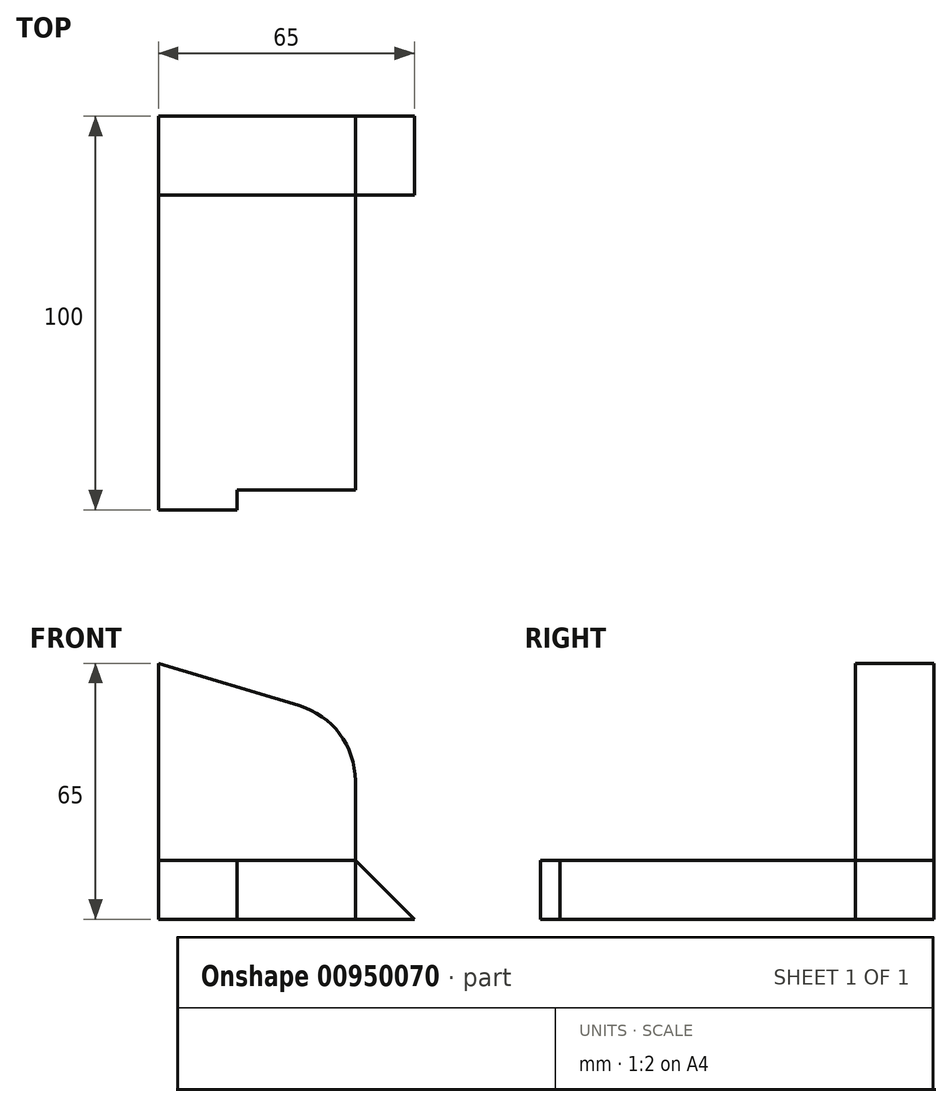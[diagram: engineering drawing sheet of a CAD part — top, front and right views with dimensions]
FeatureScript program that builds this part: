
annotation { "Feature Type Name" : "Feature", "Feature Type Description" : "" }
export const myFeature = defineFeature(function(context is Context, id is Id, definition is map)
    precondition{}
    {
        {
            var Q0;
            Q0=qCreatedBy(makeId("Top.planeOp"),FACE);
            var sketch = newSketch(context, id + "F0", { "sketchPlane" : qUnion([Q0])});
            skLineSegment(sketch, "E0.bottom", {"start": v(0, 0) * mm, "end": v(20, 0) * mm});
            skLineSegment(sketch, "E0.top", {"start": v(0, 100) * mm, "end": v(50, 100) * mm});
            skLineSegment(sketch, "E0.left", {"start": v(0, 0) * mm, "end": v(0, 100) * mm});
            skLineSegment(sketch, "E0.right", {"start": v(50, 5) * mm, "end": v(50, 100) * mm});
            skLineSegment(sketch, "E1.top", {"start": v(20, 5) * mm, "end": v(50, 5) * mm});
            skLineSegment(sketch, "E1.left", {"start": v(20, 0) * mm, "end": v(20, 5) * mm});
            skSolve(sketch);
        }
        {
            var Q0;
            Q0 = qSketchRegion(id + "F0", true);
            extrude(context, id + "F1", {"entities" : qUnion([Q0]), "depth" : 15 * mm, "offsetDistance" : 25 * mm});
        }
        {
            var Q0;
            Q0=makeQuery(id+"F1.opExtrude","SWEPT_FACE",FACE,{"disambiguationData":[OSD([sQuery(id+"F0.wireOp",EDGE,"E0.top")])]});
            var sketch = newSketch(context, id + "F2", { "sketchPlane" : qUnion([Q0])});
            skLineSegment(sketch, "E2", {"start": v(0, 15) * mm, "end": v(0, 65) * mm});
            skLineSegment(sketch, "E3", {"start": v(0, 65) * mm, "end": v(-50, 50) * mm});
            skLineSegment(sketch, "E4", {"start": v(-50, 50) * mm, "end": v(-50, 15) * mm});
            skLineSegment(sketch, "E5", {"start": v(-50, 15) * mm, "end": v(0, 15) * mm});
            skSolve(sketch);
        }
        {
            var Q0;
            Q0 = qSketchRegion(id + "F2", true);
            extrude(context, id + "F3", {"entities" : qUnion([Q0]), "operationType" : NewBodyOperationType.ADD, "oppositeDirection" : true, "depth" : 20 * mm, "offsetDistance" : 25 * mm});
        }
        {
            var Q0;
            Q0=makeQuery(id+"F3.opExtrude","SWEPT_EDGE",EDGE,{"disambiguationData":[OSD([sQuery(id+"F2.wireOp",EDGE,"E3"),sQuery(id+"F2.wireOp",EDGE,"E4")])]});
            fillet(context, id + "F4", {"entities" : qUnion([Q0]), "radius" : 20 * mm, "tangentPropagation" : true, "allowEdgeOverflow" : false});
        }
        {
            var Q0;
            Q0=makeQuery(id+"F3.boolean.opBoolean","MERGE",FACE,{"derivedFrom":[makeQuery(id+"F1.opExtrude","SWEPT_FACE",FACE,{"disambiguationData":[OSD([sQuery(id+"F0.wireOp",EDGE,"E0.top")])]}),makeQuery(id+"F3.opExtrude","CAP_FACE",FACE,{"disambiguationData":[OSD([sQuery(id+"F2.wireOp",EDGE,"E2"),sQuery(id+"F2.wireOp",EDGE,"E3"),sQuery(id+"F2.wireOp",EDGE,"E4"),sQuery(id+"F2.wireOp",EDGE,"E5")])],"isStart":true})]});
            var sketch = newSketch(context, id + "F5", { "sketchPlane" : qUnion([Q0])});
            skLineSegment(sketch, "E6", {"start": v(-50, 0) * mm, "end": v(-50, 15) * mm});
            skLineSegment(sketch, "E7", {"start": v(-50, 15) * mm, "end": v(-65, 0) * mm});
            skLineSegment(sketch, "E8", {"start": v(-65, 0) * mm, "end": v(-50, 0) * mm});
            skSolve(sketch);
        }
        {
            var Q0;
            Q0 = qSketchRegion(id + "F5", true);
            extrude(context, id + "F6", {"entities" : qUnion([Q0]), "operationType" : NewBodyOperationType.ADD, "oppositeDirection" : true, "depth" : 20 * mm, "offsetDistance" : 25 * mm});
        }
    });
